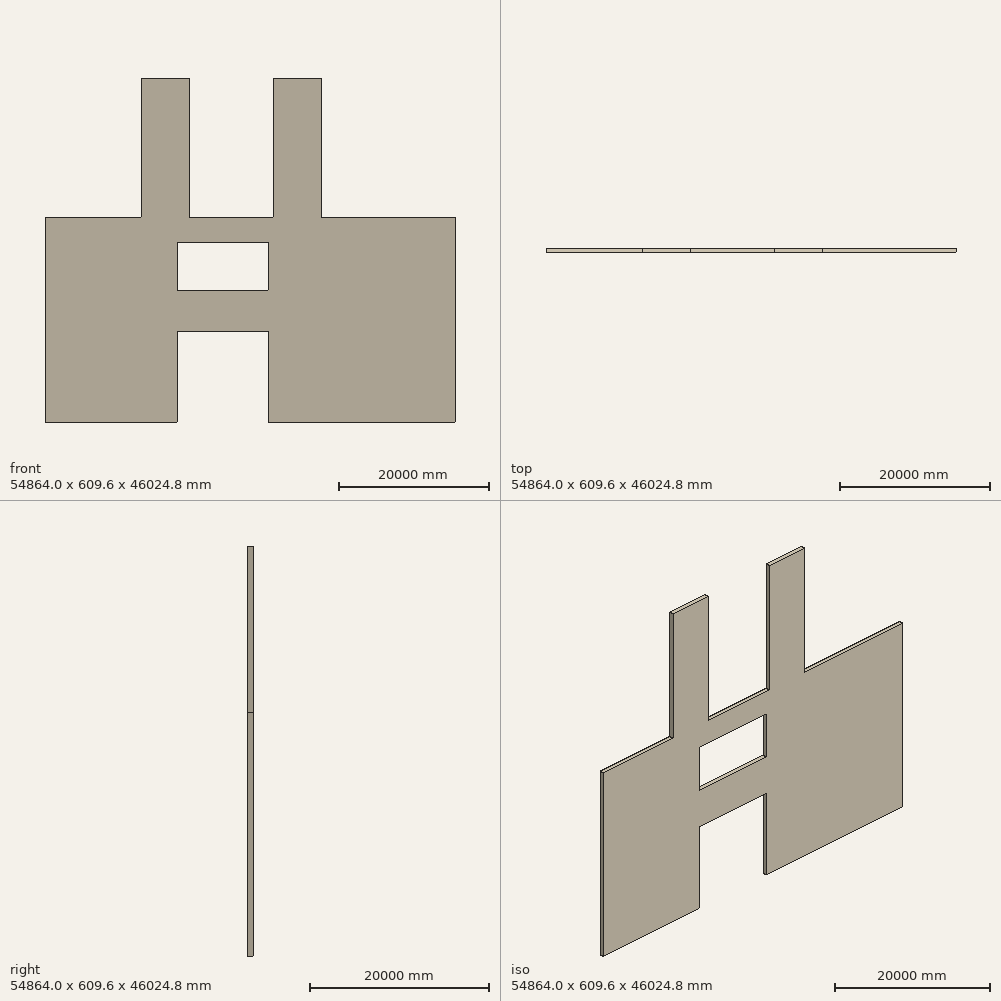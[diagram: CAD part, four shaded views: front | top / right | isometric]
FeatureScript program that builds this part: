
annotation { "Feature Type Name" : "Feature", "Feature Type Description" : "" }
export const myFeature = defineFeature(function(context is Context, id is Id, definition is map)
    precondition{}
    {
        {
            var Q0;
            Q0=qCreatedBy(makeId("Front.planeOp"),FACE);
            var sketch = newSketch(context, id + "F0", { "sketchPlane" : qUnion([Q0])});
            skPoint(sketch, "E0.orphan", {"position": v(-444.52, 0) * mm});
            skLineSegment(sketch, "E1.bottom", {"start": v(0, 0) * mm, "end": v(54864, 0) * mm});
            skLineSegment(sketch, "E1.top", {"start": v(0, 27432) * mm, "end": v(54864, 27432) * mm});
            skLineSegment(sketch, "E1.left", {"start": v(0, 0) * mm, "end": v(0, 27432) * mm});
            skLineSegment(sketch, "E1.right", {"start": v(54864, 0) * mm, "end": v(54864, 27432) * mm});
            skLineSegment(sketch, "E2.bottom", {"start": v(0, 27432) * mm, "end": v(6400.8, 27432) * mm});
            skLineSegment(sketch, "E2.top", {"start": v(0, 46024.8) * mm, "end": v(6400.8, 46024.8) * mm});
            skLineSegment(sketch, "E2.left", {"start": v(0, 27432) * mm, "end": v(0, 46024.8) * mm});
            skLineSegment(sketch, "E2.right", {"start": v(6400.8, 27432) * mm, "end": v(6400.8, 46024.8) * mm});
            skLineSegment(sketch, "E3.bottom", {"start": v(54864, 27432) * mm, "end": v(48463.2, 27432) * mm});
            skLineSegment(sketch, "E3.top", {"start": v(54864, 46024.8) * mm, "end": v(48463.2, 46024.8) * mm});
            skLineSegment(sketch, "E3.left", {"start": v(54864, 27432) * mm, "end": v(54864, 46024.8) * mm});
            skLineSegment(sketch, "E3.right", {"start": v(48463.2, 27432) * mm, "end": v(48463.2, 46024.8) * mm});
            skLineSegment(sketch, "E4", {"start": v(12801.6, 27432) * mm, "end": v(12801.6, 46024.8) * mm});
            skLineSegment(sketch, "E5", {"start": v(12801.6, 46024.8) * mm, "end": v(19202.4, 46024.8) * mm});
            skLineSegment(sketch, "E6", {"start": v(19202.4, 46024.8) * mm, "end": v(19202.4, 27432) * mm});
            skLineSegment(sketch, "E7", {"start": v(30480, 27432) * mm, "end": v(30480, 46024.8) * mm});
            skLineSegment(sketch, "E8", {"start": v(30480, 46024.8) * mm, "end": v(36880.8, 46024.8) * mm});
            skLineSegment(sketch, "E9", {"start": v(36880.8, 46024.8) * mm, "end": v(36880.8, 27432) * mm});
            skLineSegment(sketch, "E10.bottom", {"start": v(17678.4, 0) * mm, "end": v(29870.4, 0) * mm});
            skLineSegment(sketch, "E10.top", {"start": v(17678.4, 12192) * mm, "end": v(29870.4, 12192) * mm});
            skLineSegment(sketch, "E10.left", {"start": v(17678.4, 0) * mm, "end": v(17678.4, 12192) * mm});
            skLineSegment(sketch, "E10.right", {"start": v(29870.4, 0) * mm, "end": v(29870.4, 12192) * mm});
            skLineSegment(sketch, "E11.bottom", {"start": v(17678.4, 24079.2) * mm, "end": v(29870.4, 24079.2) * mm});
            skLineSegment(sketch, "E11.top", {"start": v(17678.4, 17678.4) * mm, "end": v(29870.4, 17678.4) * mm});
            skLineSegment(sketch, "E11.left", {"start": v(17678.4, 24079.2) * mm, "end": v(17678.4, 17678.4) * mm});
            skLineSegment(sketch, "E11.right", {"start": v(29870.4, 24079.2) * mm, "end": v(29870.4, 17678.4) * mm});
            skSolve(sketch);
        }
        {
            var Q0;
            Q0=makeQuery(id+"F0.imprint","IMPRINT",FACE,{"disambiguationData":[TD([[makeQuery(id+"F0.imprint","IMPRINT",EDGE,{"derivedFrom":sQuery(id+"F0.wireOp",EDGE,"E3.bottom")}),-1.0]])]});
            var Q1;
            {var subQ0=sQuery(id+"F0.wireOp",EDGE,"E7");Q1=makeQuery(id+"F0.imprint","IMPRINT",FACE,{"disambiguationData":[TD([[makeQuery(id+"F0.imprint","IMPRINT",EDGE,{"derivedFrom":subQ0}),-1.0]])]});}
            var Q2;
            {var subQ0=sQuery(id+"F0.wireOp",EDGE,"E4");Q2=makeQuery(id+"F0.imprint","IMPRINT",FACE,{"disambiguationData":[TD([[makeQuery(id+"F0.imprint","IMPRINT",EDGE,{"derivedFrom":subQ0}),-1.0]])]});}
            var Q3;
            Q3=makeQuery(id+"F0.imprint","IMPRINT",FACE,{"disambiguationData":[TD([[makeQuery(id+"F0.imprint","IMPRINT",EDGE,{"derivedFrom":sQuery(id+"F0.wireOp",EDGE,"E2.bottom")}),1.0]])]});
            var Q4;
            {var subQ2=sQuery(id+"F0.wireOp",EDGE,"E1.left");Q4=makeQuery(id+"F0.imprint","IMPRINT",FACE,{"disambiguationData":[TD([[makeQuery(id+"F0.imprint","IMPRINT",EDGE,{"derivedFrom":subQ2}),-1.0]])]});}
            extrude(context, id + "F1", {"entities" : qUnion([Q0, Q1, Q2, Q3, Q4]), "depth" : 609.6 * mm, "offsetDistance" : 30.48 * mm});
        }
    });
